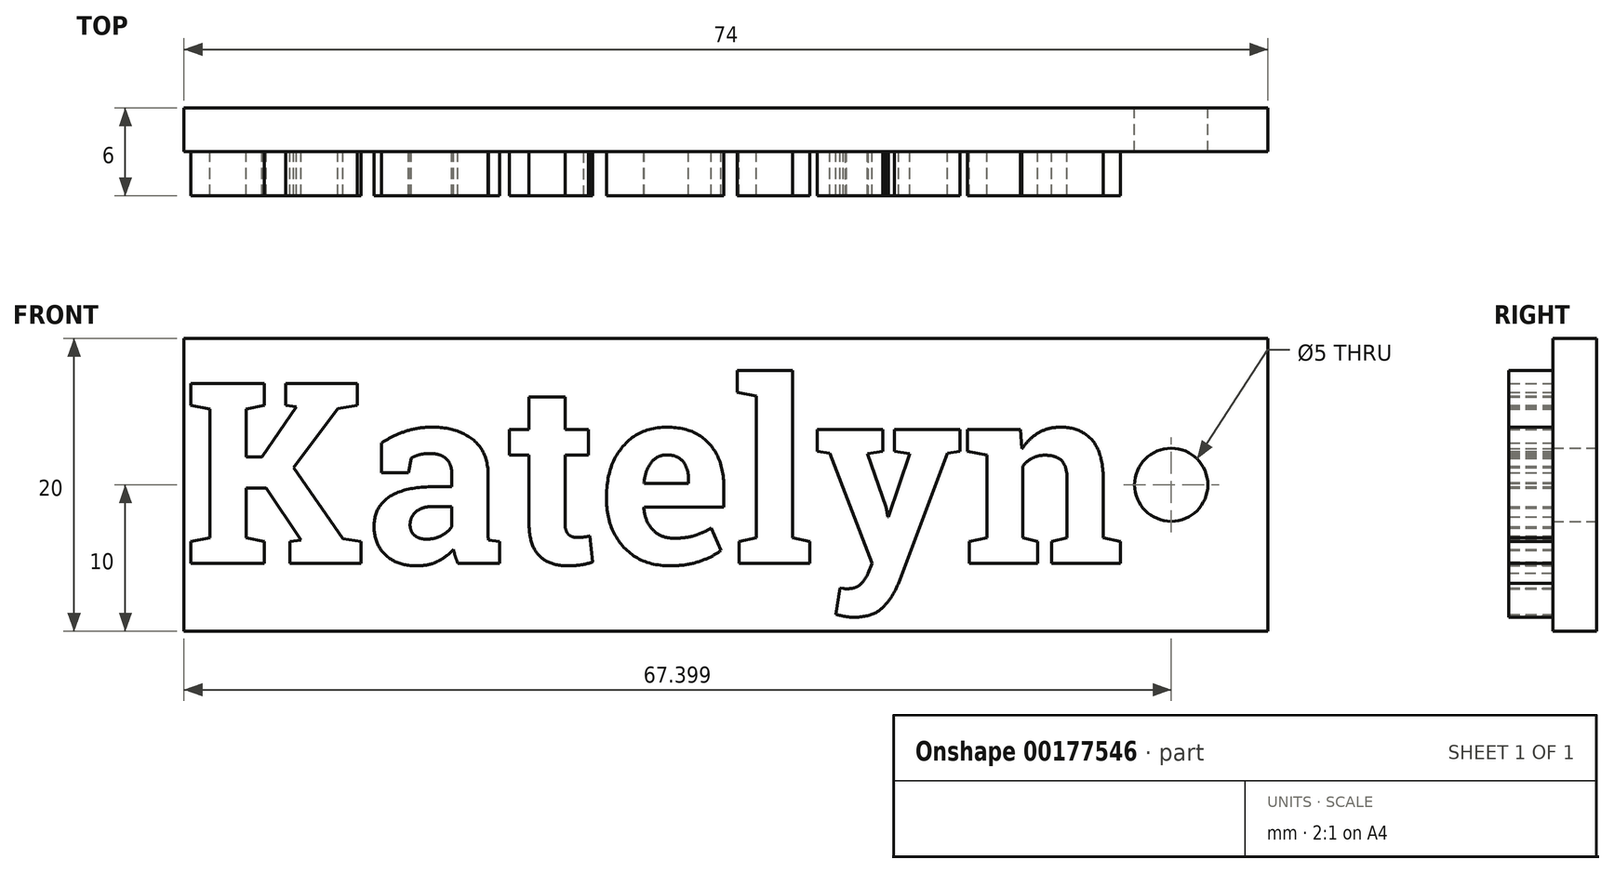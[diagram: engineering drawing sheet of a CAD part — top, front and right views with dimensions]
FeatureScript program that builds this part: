
annotation { "Feature Type Name" : "Feature", "Feature Type Description" : "" }
export const myFeature = defineFeature(function(context is Context, id is Id, definition is map)
    precondition{}
    {
        {
            var Q0;
            Q0=qCreatedBy(makeId("Front.planeOp"),FACE);
            var sketch = newSketch(context, id + "F0", { "sketchPlane" : qUnion([Q0])});
            skLineSegment(sketch, "E0.bottom", {"start": v(0, 0) * mm, "end": v(74, 0) * mm});
            skLineSegment(sketch, "E0.top", {"start": v(0, -20) * mm, "end": v(74, -20) * mm});
            skLineSegment(sketch, "E0.left", {"start": v(0, 0) * mm, "end": v(0, -20) * mm});
            skLineSegment(sketch, "E0.right", {"start": v(74, 0) * mm, "end": v(74, -20) * mm});
            skCircle(sketch, "E1", {"center": v(67.4, -10) * mm, "radius": 2.5 * mm});
            skSolve(sketch);
        }
        {
            var Q0;
            Q0 = qSketchRegion(id + "F0", true);
            extrude(context, id + "F1", {"entities" : qUnion([Q0]), "depth" : 3 * mm});
        }
        {
            var Q0;
            Q0=makeQuery(id+"F1.opExtrude","CAP_FACE",FACE,{"disambiguationData":[OSD([sQuery(id+"F0.wireOp",EDGE,"E0.bottom"),sQuery(id+"F0.wireOp",EDGE,"E0.top"),sQuery(id+"F0.wireOp",EDGE,"E0.left"),sQuery(id+"F0.wireOp",EDGE,"E0.right"),sQuery(id+"F0.wireOp",EDGE,"E1")])],"isStart":false});
            var sketch = newSketch(context, id + "F2", { "sketchPlane" : qUnion([Q0])});
            skText(sketch, "E2", { "text": "Katelyn", "fontName": "RobotoSlab-Bold.ttf"});
            const initialGuessF2  = {"E2": [0, -0.01536, 1, 0, 0.01244]};
            skSetInitialGuess(sketch, initialGuessF2);
            skSolve(sketch);
        }
        {
            var Q0;
            Q0 = qSketchRegion(id + "F2", true);
            extrude(context, id + "F3", {"entities" : qUnion([Q0]), "operationType" : NewBodyOperationType.ADD, "depth" : 3 * mm});
        }
    });
